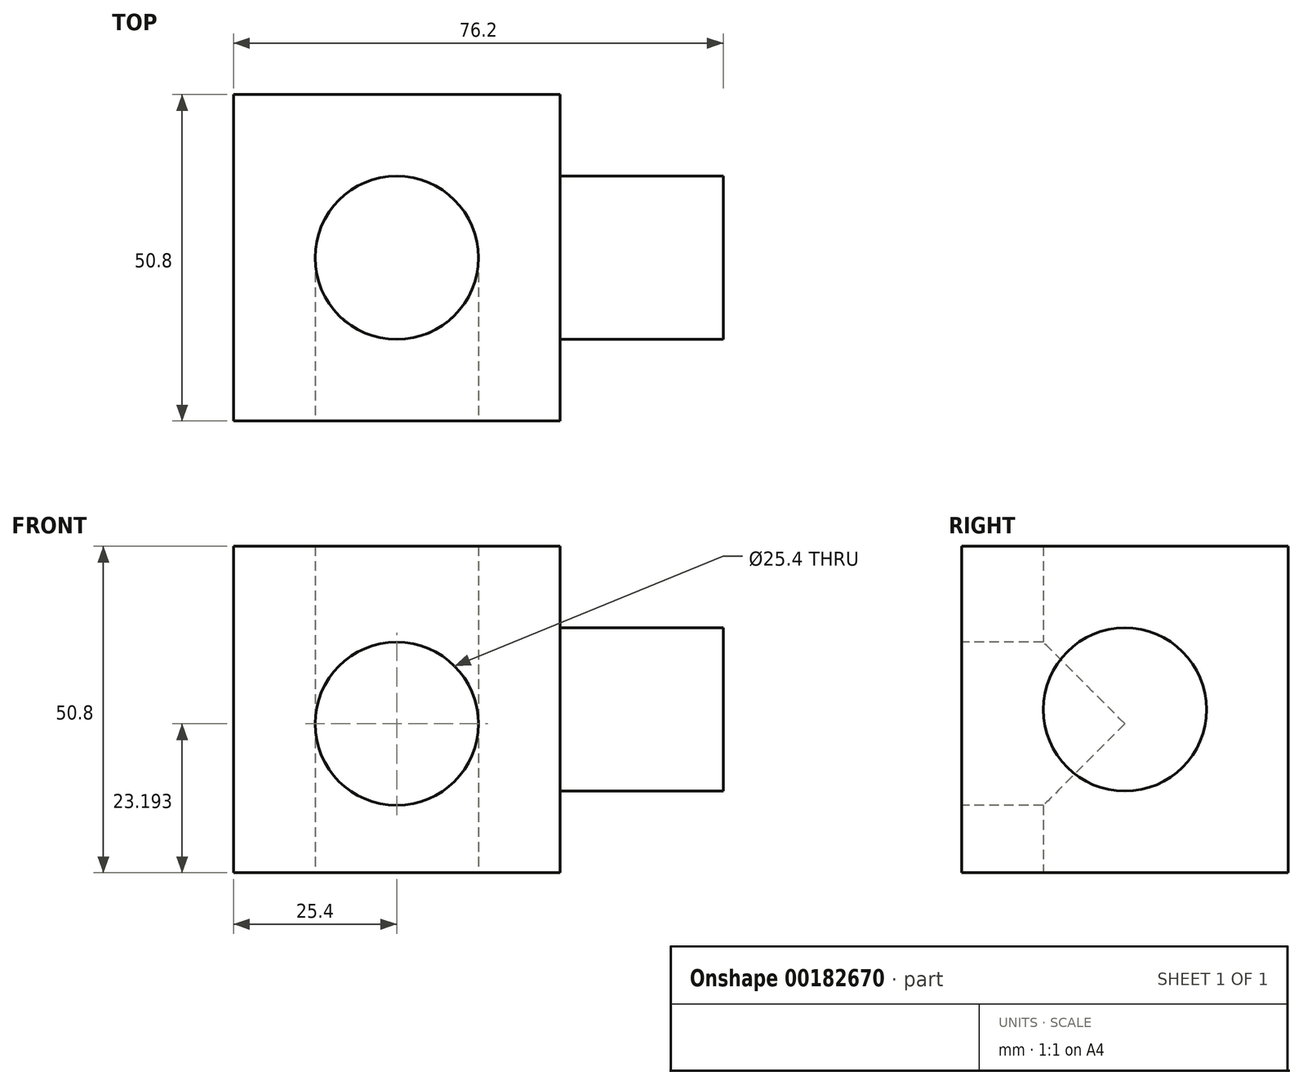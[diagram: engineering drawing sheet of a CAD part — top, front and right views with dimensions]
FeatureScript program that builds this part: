
annotation { "Feature Type Name" : "Feature", "Feature Type Description" : "" }
export const myFeature = defineFeature(function(context is Context, id is Id, definition is map)
    precondition{}
    {
        {
            var Q0;
            Q0=qCreatedBy(makeId("Top.planeOp"),FACE);
            var sketch = newSketch(context, id + "F0", { "sketchPlane" : qUnion([Q0])});
            skLineSegment(sketch, "E0.bottom", {"start": v(25.4, 25.4) * mm, "end": v(-25.4, 25.4) * mm});
            skLineSegment(sketch, "E0.top", {"start": v(25.4, -25.4) * mm, "end": v(-25.4, -25.4) * mm});
            skLineSegment(sketch, "E0.left", {"start": v(25.4, 25.4) * mm, "end": v(25.4, -25.4) * mm});
            skLineSegment(sketch, "E0.right", {"start": v(-25.4, 25.4) * mm, "end": v(-25.4, -25.4) * mm});
            skPoint(sketch, "E0.middle", {"position": v(0, 0) * mm});
            skCircle(sketch, "E1", {"center": v(0, 0) * mm, "radius": 12.7 * mm});
            skSolve(sketch);
        }
        {
            var Q0;
            Q0 = qSketchRegion(id + "F0", true);
            extrude(context, id + "F1", {"entities" : qUnion([Q0]), "depth" : 50.8 * mm});
        }
        {
            var Q0;
            Q0=makeQuery(id+"F1.opExtrude","SWEPT_FACE",FACE,{"disambiguationData":[OSD([sQuery(id+"F0.wireOp",EDGE,"E0.top")])]});
            var sketch = newSketch(context, id + "F2", { "sketchPlane" : qUnion([Q0])});
            skCircle(sketch, "E2", {"center": v(0, 23.2) * mm, "radius": 12.7 * mm});
            skSolve(sketch);
        }
        {
            var Q0;
            Q0=makeQuery(id+"F2.imprint","IMPRINT",FACE,{"disambiguationData":[TD([[makeQuery(id+"F2.imprint","IMPRINT",EDGE,{"derivedFrom":sQuery(id+"F2.wireOp",EDGE,"E2")}),1.0]])]});
            extrude(context, id + "F3", {"entities" : qUnion([Q0]), "operationType" : NewBodyOperationType.REMOVE, "oppositeDirection" : true, "depth" : 25.4 * mm});
        }
        {
            var Q0;
            Q0=makeQuery(id+"F1.opExtrude","SWEPT_FACE",FACE,{"disambiguationData":[OSD([sQuery(id+"F0.wireOp",EDGE,"E0.left")])]});
            var sketch = newSketch(context, id + "F4", { "sketchPlane" : qUnion([Q0])});
            skCircle(sketch, "E3", {"center": v(0, 25.4) * mm, "radius": 12.7 * mm});
            skPoint(sketch, "E3.centerSnap0", {"position": v(25.4, 25.4) * mm});
            skSolve(sketch);
        }
        {
            var Q0;
            Q0 = qSketchRegion(id + "F4", true);
            extrude(context, id + "F5", {"entities" : qUnion([Q0]), "operationType" : NewBodyOperationType.ADD, "depth" : 25.4 * mm});
        }
    });
